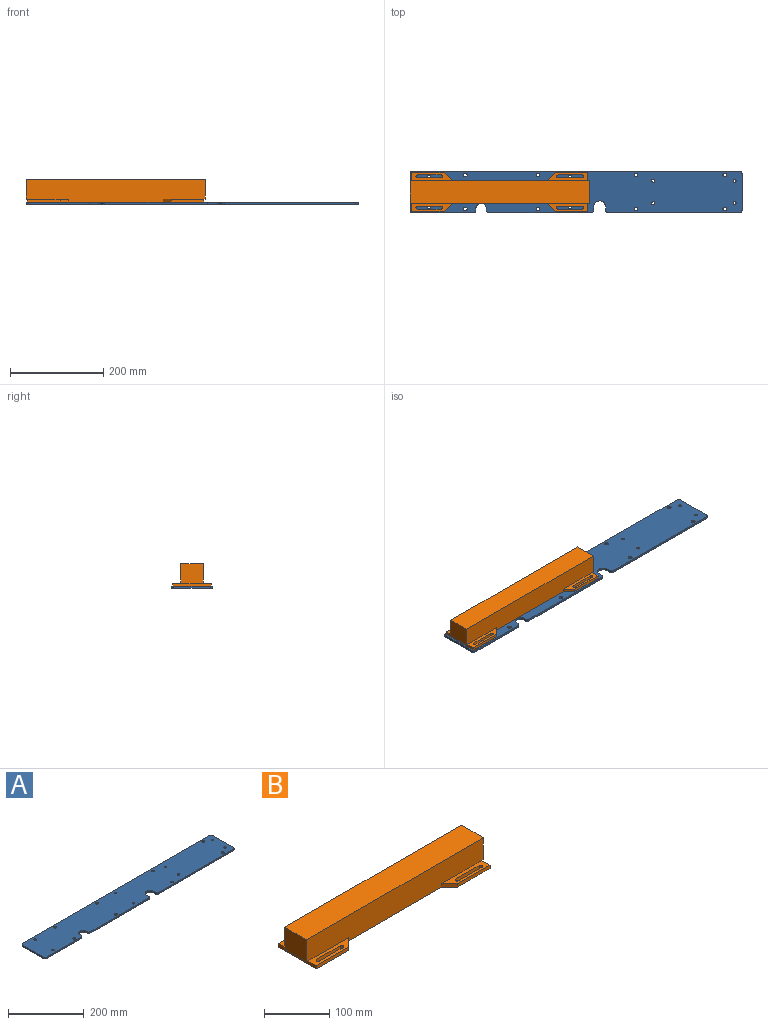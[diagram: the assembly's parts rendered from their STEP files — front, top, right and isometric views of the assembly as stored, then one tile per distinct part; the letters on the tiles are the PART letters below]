
ASSEMBLY  parts=2 mates=1
PART A: 38 faces, bbox 711.2x88.9x4.8 mm
  f0: plane 7.62x4.76mm, normal (-1,0,0), area 36.3mm2, adj f27,f28,f29,f36
  f1: plane 281.94x4.76mm, normal (0,-1,0), area 1342.7mm2, adj f28,f29,f30,f36
  f2: plane 78.74x4.76mm, normal (1,0,0), area 375mm2, adj f28,f29,f30,f31
  f3: plane 701.04x4.76mm, normal (0,1,0), area 3338.7mm2, adj f28,f29,f31,f32
  f4: plane 78.74x4.76mm, normal (-1,0,0), area 375mm2, adj f28,f29,f32,f33
  f5: plane 131.13x4.76mm, normal (0,-1,0), area 624.5mm2, adj f28,f29,f33,f34
  f6: plane 4.76x4.13mm, normal (1,0,0), area 19.7mm2, adj f7,f28,f29,f34
  f7: cylinder r=11.11mm len=22.23mm, axis (0,0,1), area 166.3mm2, adj f6,f8,f28,f29
  f8: plane 4.76x4.13mm, normal (-1,0,0), area 19.7mm2, adj f7,f28,f29,f35
  f9: plane 220.03x4.76mm, normal (0,-1,0), area 1047.9mm2, adj f28,f29,f35,f37
  f10: plane 7.62x4.76mm, normal (1,0,0), area 36.3mm2, adj f27,f28,f29,f37
  f11: cylinder r=3.17mm len=6.35mm, axis (0,0,1), area 95mm2, adj f28,f29
  f12: cylinder r=3.17mm len=6.35mm, axis (0,0,1), area 95mm2, adj f28,f29
  f13: cylinder r=3.17mm len=6.35mm, axis (0,0,1), area 95mm2, adj f28,f29
  f14: cylinder r=3.17mm len=6.35mm, axis (0,0,1), area 95mm2, adj f28,f29
  f15: cylinder r=3.17mm len=6.35mm, axis (0,0,1), area 95mm2, adj f28,f29
  f16: cylinder r=3.17mm len=6.35mm, axis (0,0,1), area 95mm2, adj f28,f29
  f17: cylinder r=3.17mm len=6.35mm, axis (0,0,1), area 95mm2, adj f28,f29
  f18: cylinder r=3.97mm len=7.94mm, axis (0,0,1), area 118.8mm2, adj f28,f29
  f19: cylinder r=3.97mm len=7.94mm, axis (0,0,1), area 118.8mm2, adj f28,f29
  f20: cylinder r=3.97mm len=7.94mm, axis (0,0,1), area 118.8mm2, adj f28,f29
  f21: cylinder r=3.97mm len=7.94mm, axis (0,0,1), area 118.8mm2, adj f28,f29
  f22: cylinder r=3.97mm len=7.94mm, axis (0,0,1), area 118.8mm2, adj f28,f29
  f23: cylinder r=3.97mm len=7.94mm, axis (0,0,1), area 118.8mm2, adj f28,f29
  f24: cylinder r=3.97mm len=7.94mm, axis (0,0,1), area 118.8mm2, adj f28,f29
  f25: cylinder r=3.97mm len=7.94mm, axis (0,0,1), area 118.8mm2, adj f28,f29
  f26: cylinder r=3.17mm len=6.35mm, axis (0,0,1), area 95mm2, adj f28,f29
  f27: cylinder r=12.7mm len=25.4mm, axis (0,0,1), area 190mm2, adj f0,f10,f28,f29
  f28: plane 711.2x88.9mm, normal (0,0,-1), area 61557.6mm2, adj f0,f1,f2,f3,f4,f5,f6,f7
  f29: plane 711.2x88.9mm, normal (0,0,1), area 61557.6mm2, adj f0,f1,f2,f3,f4,f5,f6,f7
  f30: cylinder r=5.08mm len=5.08mm, axis (0,0,1), area 38mm2, adj f1,f2,f28,f29
  f31: cylinder r=5.08mm len=5.08mm, axis (0,0,-1), area 38mm2, adj f2,f3,f28,f29
  f32: cylinder r=5.08mm len=5.08mm, axis (0,0,1), area 38mm2, adj f3,f4,f28,f29
  f33: cylinder r=5.08mm len=5.08mm, axis (0,0,-1), area 38mm2, adj f4,f5,f28,f29
  f34: cylinder r=5.08mm len=5.08mm, axis (0,0,1), area 38mm2, adj f5,f6,f28,f29
  f35: cylinder r=5.08mm len=5.08mm, axis (0,0,-1), area 38mm2, adj f8,f9,f28,f29
  f36: cylinder r=5.08mm len=5.08mm, axis (0,0,-1), area 38mm2, adj f0,f1,f28,f29
  f37: cylinder r=5.08mm len=5.08mm, axis (0,0,1), area 38mm2, adj f9,f10,f28,f29
PART B: 38 faces, bbox 384.2x82.6x47.6 mm
  f0: plane 82.55x6.35mm, normal (-1,0,0), area 524.2mm2, adj f3,f4,f30,f31,f32,f36
  f1: plane 87.31x17.46mm, normal (0,0,1), area 1018mm2, adj f9,f10,f11,f12,f14,f15,f16,f26
  f2: plane 87.31x17.46mm, normal (0,0,1), area 1018mm2, adj f6,f7,f8,f9,f17,f18,f19,f27
  f3: plane 87.31x17.46mm, normal (0,0,1), area 1018mm2, adj f0,f4,f5,f6,f20,f21,f22,f28
  f4: plane 69.85x6.35mm, normal (0,-1,0), area 443.5mm2, adj f0,f3,f5,f32
  f5: plane 17.46x17.46mm, normal (0.71,-0.71,0), area 156.8mm2, adj f3,f4,f6,f32
  f6: plane 384.18x47.63mm, normal (0,-1,0), area 17147.1mm2, adj f2,f3,f5,f7,f32,f33,f34,f35
  f7: plane 17.46x17.46mm, normal (-0.71,-0.71,0), area 156.8mm2, adj f2,f6,f8,f32
  f8: plane 69.85x6.35mm, normal (0,-1,0), area 443.5mm2, adj f2,f7,f9,f32
  f9: plane 82.55x6.35mm, normal (1,0,0), area 524.2mm2, adj f1,f2,f8,f10,f32,f34
  f10: plane 69.85x6.35mm, normal (0,1,0), area 443.5mm2, adj f1,f9,f11,f32
  f11: plane 17.46x17.46mm, normal (-0.71,0.71,0), area 156.8mm2, adj f1,f10,f12,f32
  f12: plane 384.18x47.63mm, normal (0,1,0), area 17147.1mm2, adj f1,f11,f13,f31,f32,f33,f34,f35
  f13: plane 17.46x17.46mm, normal (0.71,0.71,0), area 156.8mm2, adj f12,f30,f31,f32
  f14: cylinder r=3.17mm len=6.35mm, axis (0,0,-1), area 63.3mm2, adj f1,f15,f26,f32
  f15: plane 50.8x6.35mm, normal (0,1,0), area 322.6mm2, adj f1,f14,f16,f32
  f16: cylinder r=3.17mm len=6.35mm, axis (0,0,-1), area 63.3mm2, adj f1,f15,f26,f32
  f17: plane 50.8x6.35mm, normal (0,-1,0), area 322.6mm2, adj f2,f18,f27,f32
  f18: cylinder r=3.17mm len=6.35mm, axis (0,0,-1), area 63.3mm2, adj f2,f17,f19,f32
  f19: plane 50.8x6.35mm, normal (0,1,0), area 322.6mm2, adj f2,f18,f27,f32
  f20: cylinder r=3.17mm len=6.35mm, axis (0,0,-1), area 63.3mm2, adj f3,f21,f28,f32
  f21: plane 50.8x6.35mm, normal (0,-1,0), area 322.6mm2, adj f3,f20,f22,f32
  f22: cylinder r=3.17mm len=6.35mm, axis (0,0,-1), area 63.3mm2, adj f3,f21,f28,f32
  f23: cylinder r=3.17mm len=6.35mm, axis (0,0,-1), area 63.3mm2, adj f24,f29,f31,f32
  f24: plane 50.8x6.35mm, normal (0,-1,0), area 322.6mm2, adj f23,f25,f31,f32
  f25: cylinder r=3.17mm len=6.35mm, axis (0,0,-1), area 63.3mm2, adj f24,f29,f31,f32
  f26: plane 50.8x6.35mm, normal (0,-1,0), area 322.6mm2, adj f1,f14,f16,f32
  f27: cylinder r=3.17mm len=6.35mm, axis (0,0,-1), area 63.3mm2, adj f2,f17,f19,f32
  f28: plane 50.8x6.35mm, normal (0,1,0), area 322.6mm2, adj f3,f20,f22,f32
  f29: plane 50.8x6.35mm, normal (0,1,0), area 322.6mm2, adj f23,f25,f31,f32
  f30: plane 69.85x6.35mm, normal (0,1,0), area 443.5mm2, adj f0,f13,f31,f32
  f31: plane 87.31x17.46mm, normal (0,0,1), area 1018mm2, adj f0,f12,f13,f23,f24,f25,f29,f30
  f32: plane 377.83x82.55mm, normal (0,0,-1), area 22065.8mm2, adj f0,f4,f5,f6,f7,f8,f9,f10
  f33: plane 384.18x47.63mm, normal (0,0,1), area 18296.3mm2, adj f6,f12,f35,f37
  f34: plane 47.63x3.18mm, normal (0,0,-1), area 151.2mm2, adj f6,f9,f12,f35
  f35: plane 47.63x41.28mm, normal (1,0,0), area 1965.7mm2, adj f6,f12,f33,f34
  f36: plane 47.63x3.18mm, normal (0,0,-1), area 151.2mm2, adj f0,f6,f12,f37
  f37: plane 47.63x41.28mm, normal (-1,0,0), area 1965.7mm2, adj f6,f12,f33,f36
PLACE A t=(-6.53,47.96,-12.22)mm
PLACE B t=(-3.37,51.08,-12.22)mm
MATE planar A.f29 <-> B.f32  axis (0,0,1) through (349.54,92.96,-12.22)mm
